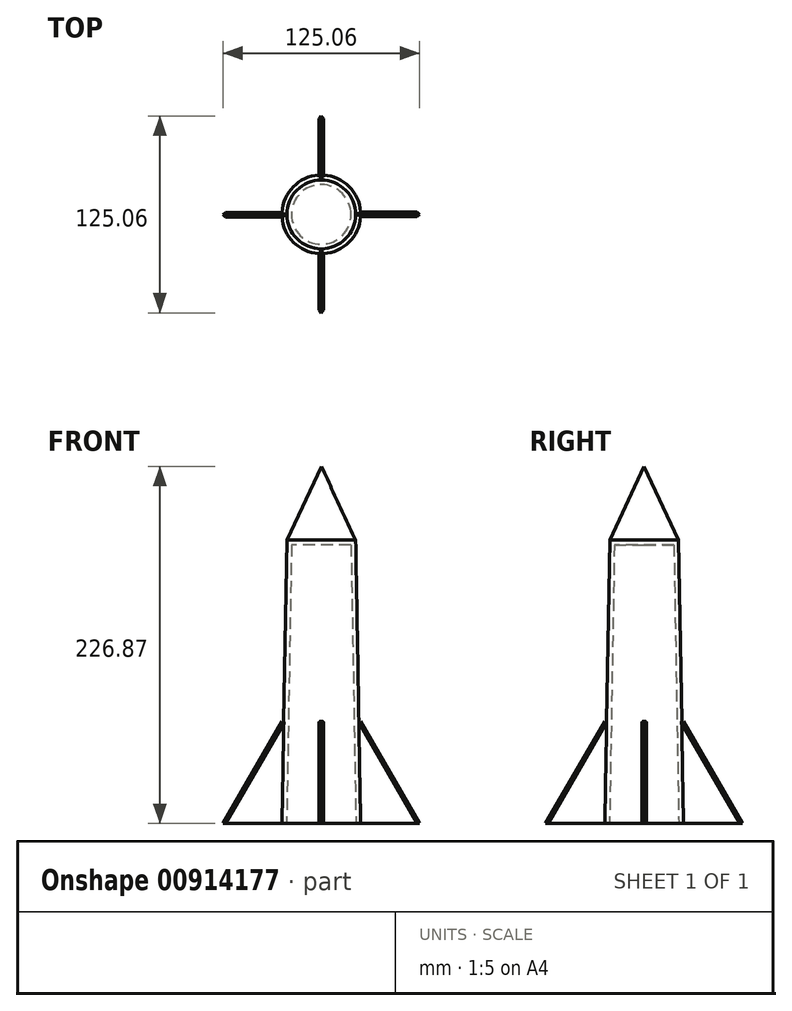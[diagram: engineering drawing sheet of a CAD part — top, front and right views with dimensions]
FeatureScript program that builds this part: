
annotation { "Feature Type Name" : "Feature", "Feature Type Description" : "" }
export const myFeature = defineFeature(function(context is Context, id is Id, definition is map)
    precondition{}
    {
        {
            var Q0;
            Q0=qCreatedBy(makeId("Top.planeOp"),FACE);
            var sketch = newSketch(context, id + "F0", { "sketchPlane" : qUnion([Q0])});
            skCircle(sketch, "E0", {"center": v(0, 0) * mm, "radius": 25 * mm});
            skSolve(sketch);
        }
        {
            var Q0;
            Q0=makeQuery(id+"F0.imprint","IMPRINT",FACE,{"disambiguationData":[TD([[makeQuery(id+"F0.imprint","IMPRINT",EDGE,{"derivedFrom":sQuery(id+"F0.wireOp",EDGE,"E0")}),1.0]])]});
            extrude(context, id + "F1", {"entities" : qUnion([Q0]), "depth" : 180 * mm, "offsetDistance" : 25 * mm, "hasDraft" : true, "draftAngle" : 1 * degree, "draftPullDirection" : true});
        }
        {
            var Q0;
            Q0=qCreatedBy(makeId("Top.planeOp"),FACE);
            var sketch = newSketch(context, id + "F2", { "sketchPlane" : qUnion([Q0])});
            skLineSegment(sketch, "E1.bottom", {"start": v(1.43, 0) * mm, "end": v(-1.57, 0) * mm});
            skLineSegment(sketch, "E1.top", {"start": v(1.43, 65) * mm, "end": v(-1.57, 65) * mm});
            skLineSegment(sketch, "E1.left", {"start": v(1.43, 0) * mm, "end": v(1.43, 65) * mm});
            skLineSegment(sketch, "E1.right", {"start": v(-1.57, 0) * mm, "end": v(-1.57, 65) * mm});
            skSolve(sketch);
        }
        {
            var Q0;
            Q0=makeQuery(id+"F2.imprint","IMPRINT",FACE,{"disambiguationData":[TD([[makeQuery(id+"F2.imprint","IMPRINT",EDGE,{"derivedFrom":sQuery(id+"F2.wireOp",EDGE,"E1.bottom")}),-1.0]])]});
            extrude(context, id + "F3", {"entities" : qUnion([Q0]), "operationType" : NewBodyOperationType.ADD, "depth" : 65 * mm, "offsetDistance" : 25 * mm});
        }
        {
            var Q0;
            Q0=makeQuery(id+"F3.opExtrude","CAP_EDGE",EDGE,{"disambiguationData":[OSD([sQuery(id+"F2.wireOp",EDGE,"E1.top")])],"isStart":false});
            chamfer(context, id + "F4", {"entities" : qUnion([Q0]), "chamferType" : ChamferType.OFFSET_ANGLE, "width" : 40 * mm, "oppositeDirection" : false, "angle" : 60 * degree, "tangentPropagation" : true});
        }
        {
            var Q0;
            Q0=makeQuery(id+"F4.opChamfer","BLEND_EDGE",EDGE,{"blendedFrom":[makeQuery(id+"F3.opExtrude","CAP_EDGE",EDGE,{"disambiguationData":[OSD([sQuery(id+"F2.wireOp",EDGE,"E1.top")])],"isStart":false}),makeQuery(id+"F3.opExtrude","SWEPT_FACE",FACE,{"disambiguationData":[OSD([sQuery(id+"F2.wireOp",EDGE,"E1.right")])]})],"blendedInto":[makeQuery(id+"F3.opExtrude","SWEPT_FACE",FACE,{"disambiguationData":[OSD([sQuery(id+"F2.wireOp",EDGE,"E1.right")])]})]});
            chamfer(context, id + "F5", {"entities" : qUnion([Q0]), "width" : 1.5 * mm, "tangentPropagation" : true});
        }
        {
            var Q0;
            Q0=makeQuery(id+"F4.opChamfer","BLEND_EDGE",EDGE,{"blendedFrom":[makeQuery(id+"F3.opExtrude","CAP_EDGE",EDGE,{"disambiguationData":[OSD([sQuery(id+"F2.wireOp",EDGE,"E1.top")])],"isStart":false}),makeQuery(id+"F3.opExtrude","SWEPT_FACE",FACE,{"disambiguationData":[OSD([sQuery(id+"F2.wireOp",EDGE,"E1.left")])]})],"blendedInto":[makeQuery(id+"F3.opExtrude","SWEPT_FACE",FACE,{"disambiguationData":[OSD([sQuery(id+"F2.wireOp",EDGE,"E1.left")])]})]});
            chamfer(context, id + "F6", {"entities" : qUnion([Q0]), "width" : 1.5 * mm, "tangentPropagation" : true});
        }
        {
            var Q0;
            Q0=qCreatedBy(makeId("Top.planeOp"),FACE);
            var sketch = newSketch(context, id + "F7", { "sketchPlane" : qUnion([Q0])});
            skLineSegment(sketch, "E2.bottom", {"start": v(-1.54, 0) * mm, "end": v(1.46, 0) * mm});
            skLineSegment(sketch, "E2.top", {"start": v(-1.54, -65) * mm, "end": v(1.46, -65) * mm});
            skLineSegment(sketch, "E2.left", {"start": v(-1.54, 0) * mm, "end": v(-1.54, -65) * mm});
            skLineSegment(sketch, "E2.right", {"start": v(1.46, 0) * mm, "end": v(1.46, -65) * mm});
            skSolve(sketch);
        }
        {
            var Q0;
            Q0=makeQuery(id+"F7.imprint","IMPRINT",FACE,{"disambiguationData":[TD([[makeQuery(id+"F7.imprint","IMPRINT",EDGE,{"derivedFrom":sQuery(id+"F7.wireOp",EDGE,"E2.bottom")}),-1.0]])]});
            extrude(context, id + "F8", {"entities" : qUnion([Q0]), "operationType" : NewBodyOperationType.ADD, "depth" : 65 * mm, "offsetDistance" : 25 * mm});
        }
        {
            var Q0;
            Q0=makeQuery(id+"F8.opExtrude","CAP_EDGE",EDGE,{"disambiguationData":[OSD([sQuery(id+"F7.wireOp",EDGE,"E2.top")])],"isStart":false});
            chamfer(context, id + "F9", {"entities" : qUnion([Q0]), "chamferType" : ChamferType.OFFSET_ANGLE, "width" : 40 * mm, "oppositeDirection" : false, "angle" : 60 * degree, "tangentPropagation" : true});
        }
        {
            var Q0;
            Q0=makeQuery(id+"F9.opChamfer","BLEND_EDGE",EDGE,{"blendedFrom":[makeQuery(id+"F8.opExtrude","CAP_EDGE",EDGE,{"disambiguationData":[OSD([sQuery(id+"F7.wireOp",EDGE,"E2.top")])],"isStart":false}),makeQuery(id+"F8.opExtrude","SWEPT_FACE",FACE,{"disambiguationData":[OSD([sQuery(id+"F7.wireOp",EDGE,"E2.left")])]})],"blendedInto":[makeQuery(id+"F8.opExtrude","SWEPT_FACE",FACE,{"disambiguationData":[OSD([sQuery(id+"F7.wireOp",EDGE,"E2.left")])]})]});
            chamfer(context, id + "F10", {"entities" : qUnion([Q0]), "width" : 1.5 * mm, "tangentPropagation" : true});
        }
        {
            var Q0;
            Q0=makeQuery(id+"F9.opChamfer","BLEND_EDGE",EDGE,{"blendedFrom":[makeQuery(id+"F8.opExtrude","CAP_EDGE",EDGE,{"disambiguationData":[OSD([sQuery(id+"F7.wireOp",EDGE,"E2.top")])],"isStart":false}),makeQuery(id+"F8.opExtrude","SWEPT_FACE",FACE,{"disambiguationData":[OSD([sQuery(id+"F7.wireOp",EDGE,"E2.right")])]})],"blendedInto":[makeQuery(id+"F8.opExtrude","SWEPT_FACE",FACE,{"disambiguationData":[OSD([sQuery(id+"F7.wireOp",EDGE,"E2.right")])]})]});
            chamfer(context, id + "F11", {"entities" : qUnion([Q0]), "width" : 1.5 * mm, "tangentPropagation" : true});
        }
        {
            var Q0;
            Q0=qCreatedBy(makeId("Top.planeOp"),FACE);
            var sketch = newSketch(context, id + "F12", { "sketchPlane" : qUnion([Q0])});
            skLineSegment(sketch, "E3.bottom", {"start": v(0, -1.72) * mm, "end": v(-65, -1.72) * mm});
            skLineSegment(sketch, "E3.top", {"start": v(0, 1.28) * mm, "end": v(-65, 1.28) * mm});
            skLineSegment(sketch, "E3.left", {"start": v(0, -1.72) * mm, "end": v(0, 1.28) * mm});
            skLineSegment(sketch, "E3.right", {"start": v(-65, -1.72) * mm, "end": v(-65, 1.28) * mm});
            skSolve(sketch);
        }
        {
            var Q0;
            Q0=makeQuery(id+"F12.imprint","IMPRINT",FACE,{"disambiguationData":[TD([[makeQuery(id+"F12.imprint","IMPRINT",EDGE,{"derivedFrom":sQuery(id+"F12.wireOp",EDGE,"E3.bottom")}),-1.0]])]});
            extrude(context, id + "F13", {"entities" : qUnion([Q0]), "operationType" : NewBodyOperationType.ADD, "depth" : 65 * mm, "offsetDistance" : 25 * mm});
        }
        {
            var Q0;
            Q0=makeQuery(id+"F13.opExtrude","CAP_EDGE",EDGE,{"disambiguationData":[OSD([sQuery(id+"F12.wireOp",EDGE,"E3.right")])],"isStart":false});
            chamfer(context, id + "F14", {"entities" : qUnion([Q0]), "chamferType" : ChamferType.OFFSET_ANGLE, "width" : 40 * mm, "oppositeDirection" : true, "angle" : 60 * degree, "tangentPropagation" : true});
        }
        {
            var Q0;
            Q0=makeQuery(id+"F14.opChamfer","BLEND_EDGE",EDGE,{"blendedFrom":[makeQuery(id+"F13.opExtrude","CAP_EDGE",EDGE,{"disambiguationData":[OSD([sQuery(id+"F12.wireOp",EDGE,"E3.right")])],"isStart":false}),makeQuery(id+"F13.opExtrude","SWEPT_FACE",FACE,{"disambiguationData":[OSD([sQuery(id+"F12.wireOp",EDGE,"E3.top")])]})],"blendedInto":[makeQuery(id+"F13.opExtrude","SWEPT_FACE",FACE,{"disambiguationData":[OSD([sQuery(id+"F12.wireOp",EDGE,"E3.top")])]})]});
            var Q1;
            Q1=makeQuery(id+"F14.opChamfer","BLEND_EDGE",EDGE,{"blendedFrom":[makeQuery(id+"F13.opExtrude","CAP_EDGE",EDGE,{"disambiguationData":[OSD([sQuery(id+"F12.wireOp",EDGE,"E3.right")])],"isStart":false}),makeQuery(id+"F13.opExtrude","SWEPT_FACE",FACE,{"disambiguationData":[OSD([sQuery(id+"F12.wireOp",EDGE,"E3.bottom")])]})],"blendedInto":[makeQuery(id+"F13.opExtrude","SWEPT_FACE",FACE,{"disambiguationData":[OSD([sQuery(id+"F12.wireOp",EDGE,"E3.bottom")])]})]});
            chamfer(context, id + "F15", {"entities" : qUnion([Q0, Q1]), "width" : 1.5 * mm, "tangentPropagation" : true});
        }
        {
            var Q0;
            Q0=qCreatedBy(makeId("Top.planeOp"),FACE);
            var sketch = newSketch(context, id + "F16", { "sketchPlane" : qUnion([Q0])});
            skLineSegment(sketch, "E4.bottom", {"start": v(0, 1.56) * mm, "end": v(65, 1.56) * mm});
            skLineSegment(sketch, "E4.top", {"start": v(0, -1.44) * mm, "end": v(65, -1.44) * mm});
            skLineSegment(sketch, "E4.left", {"start": v(0, 1.56) * mm, "end": v(0, -1.44) * mm});
            skLineSegment(sketch, "E4.right", {"start": v(65, 1.56) * mm, "end": v(65, -1.44) * mm});
            skSolve(sketch);
        }
        {
            var Q0;
            Q0=makeQuery(id+"F16.imprint","IMPRINT",FACE,{"disambiguationData":[TD([[makeQuery(id+"F16.imprint","IMPRINT",EDGE,{"derivedFrom":sQuery(id+"F16.wireOp",EDGE,"E4.bottom")}),-1.0]])]});
            extrude(context, id + "F17", {"entities" : qUnion([Q0]), "operationType" : NewBodyOperationType.ADD, "depth" : 65 * mm, "offsetDistance" : 25 * mm});
        }
        {
            var Q0;
            Q0=makeQuery(id+"F17.opExtrude","CAP_EDGE",EDGE,{"disambiguationData":[OSD([sQuery(id+"F16.wireOp",EDGE,"E4.right")])],"isStart":false});
            chamfer(context, id + "F18", {"entities" : qUnion([Q0]), "chamferType" : ChamferType.OFFSET_ANGLE, "width" : 40 * mm, "oppositeDirection" : true, "angle" : 60 * degree, "tangentPropagation" : true});
        }
        {
            var Q0;
            Q0=makeQuery(id+"F18.opChamfer","BLEND_EDGE",EDGE,{"blendedFrom":[makeQuery(id+"F17.opExtrude","CAP_EDGE",EDGE,{"disambiguationData":[OSD([sQuery(id+"F16.wireOp",EDGE,"E4.right")])],"isStart":false}),makeQuery(id+"F17.opExtrude","SWEPT_FACE",FACE,{"disambiguationData":[OSD([sQuery(id+"F16.wireOp",EDGE,"E4.top")])]})],"blendedInto":[makeQuery(id+"F17.opExtrude","SWEPT_FACE",FACE,{"disambiguationData":[OSD([sQuery(id+"F16.wireOp",EDGE,"E4.top")])]})]});
            chamfer(context, id + "F19", {"entities" : qUnion([Q0]), "width" : 1.5 * mm, "tangentPropagation" : true});
        }
        {
            var Q0;
            Q0=makeQuery(id+"F18.opChamfer","BLEND_EDGE",EDGE,{"blendedFrom":[makeQuery(id+"F17.opExtrude","CAP_EDGE",EDGE,{"disambiguationData":[OSD([sQuery(id+"F16.wireOp",EDGE,"E4.right")])],"isStart":false}),makeQuery(id+"F17.opExtrude","SWEPT_FACE",FACE,{"disambiguationData":[OSD([sQuery(id+"F16.wireOp",EDGE,"E4.bottom")])]})],"blendedInto":[makeQuery(id+"F17.opExtrude","SWEPT_FACE",FACE,{"disambiguationData":[OSD([sQuery(id+"F16.wireOp",EDGE,"E4.bottom")])]})]});
            chamfer(context, id + "F20", {"entities" : qUnion([Q0]), "width" : 1.5 * mm, "tangentPropagation" : true});
        }
        {
            var Q0;
            Q0=makeQuery(id+"F17.boolean.opBoolean","MERGE",FACE,{"derivedFrom":[makeQuery(id+"F13.boolean.opBoolean","MERGE",FACE,{"derivedFrom":[makeQuery(id+"F8.boolean.opBoolean","MERGE",FACE,{"derivedFrom":[makeQuery(id+"F3.boolean.opBoolean","MERGE",FACE,{"derivedFrom":[makeQuery(id+"F1.opExtrude","CAP_FACE",FACE,{"disambiguationData":[OSD([sQuery(id+"F0.wireOp",EDGE,"E0")])],"isStart":true}),makeQuery(id+"F3.opExtrude","CAP_FACE",FACE,{"disambiguationData":[OSD([sQuery(id+"F2.wireOp",EDGE,"E1.bottom"),sQuery(id+"F2.wireOp",EDGE,"E1.top"),sQuery(id+"F2.wireOp",EDGE,"E1.left"),sQuery(id+"F2.wireOp",EDGE,"E1.right")])],"isStart":true})]}),makeQuery(id+"F8.opExtrude","CAP_FACE",FACE,{"disambiguationData":[OSD([sQuery(id+"F7.wireOp",EDGE,"E2.bottom"),sQuery(id+"F7.wireOp",EDGE,"E2.top"),sQuery(id+"F7.wireOp",EDGE,"E2.left"),sQuery(id+"F7.wireOp",EDGE,"E2.right")])],"isStart":true})]}),makeQuery(id+"F13.opExtrude","CAP_FACE",FACE,{"disambiguationData":[OSD([sQuery(id+"F12.wireOp",EDGE,"E3.bottom"),sQuery(id+"F12.wireOp",EDGE,"E3.top"),sQuery(id+"F12.wireOp",EDGE,"E3.left"),sQuery(id+"F12.wireOp",EDGE,"E3.right")])],"isStart":true})]}),makeQuery(id+"F17.opExtrude","CAP_FACE",FACE,{"disambiguationData":[OSD([sQuery(id+"F16.wireOp",EDGE,"E4.bottom"),sQuery(id+"F16.wireOp",EDGE,"E4.top"),sQuery(id+"F16.wireOp",EDGE,"E4.left"),sQuery(id+"F16.wireOp",EDGE,"E4.right")])],"isStart":true})]});
            shell(context, id + "F21", {"entities" : qUnion([Q0]), "thickness" : 3 * mm});
        }
        {
            var Q0;
            Q0=makeQuery(id+"F1.opExtrude","CAP_FACE",FACE,{"disambiguationData":[OSD([sQuery(id+"F0.wireOp",EDGE,"E0")])],"isStart":false});
            extrude(context, id + "F22", {"entities" : qUnion([Q0]), "operationType" : NewBodyOperationType.ADD, "depth" : 55 * mm, "offsetDistance" : 25 * mm, "hasDraft" : true, "draftAngle" : 25 * degree, "draftPullDirection" : true});
        }
    });
